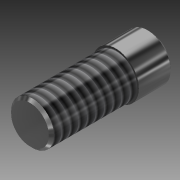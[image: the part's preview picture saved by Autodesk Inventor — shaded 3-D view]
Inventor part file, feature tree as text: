
AUTODESK INVENTOR PART (.ipt)
format: ipt  version: 2018 (Build 220112000, 112)  size: 110,592 bytes
history: native  units: mm (DEFAULTED — no unit token found)
features: extrude x2, chamfer x2, sketch x2, thread x1, reference x1
ambient origin geometry x8: Origin, YZ Plane, XZ Plane, XY Plane, X Axis, Y Axis, Z Axis, Center Point
bodies: Solid1 (feature_tree)
feature tree (8):
  extrude  "Extrusion1"  Depth=5.08mm TaperAngle=0.0deg
  chamfer  "Chamfer1"  Distance=3.175mm
  extrude  "Extrusion2"  Depth=12.7mm TaperAngle=0.0deg
  chamfer  "Chamfer2"  Distance=3.175mm
  thread  "Thread1"  [1 undecoded]
  sketch  "Sketch1"  dims[d0=6.858mm d1=5.08mm d2=0.0mm d3=0.381mm d4=3.175mm]
  reference  "Reference1"
  sketch  "Sketch2"  dims[d5=6.35mm d6=12.7mm d7=0.0mm d8=0.381mm d9=3.175mm d10=25.4mm d11=0.0mm d12=45.0deg d13=45.0deg]
note: 1 required parameter value undecoded (feature->parameter linkage not recoverable at this tier; creation-order binding heuristic only, values carry confidence <= 0.55)
